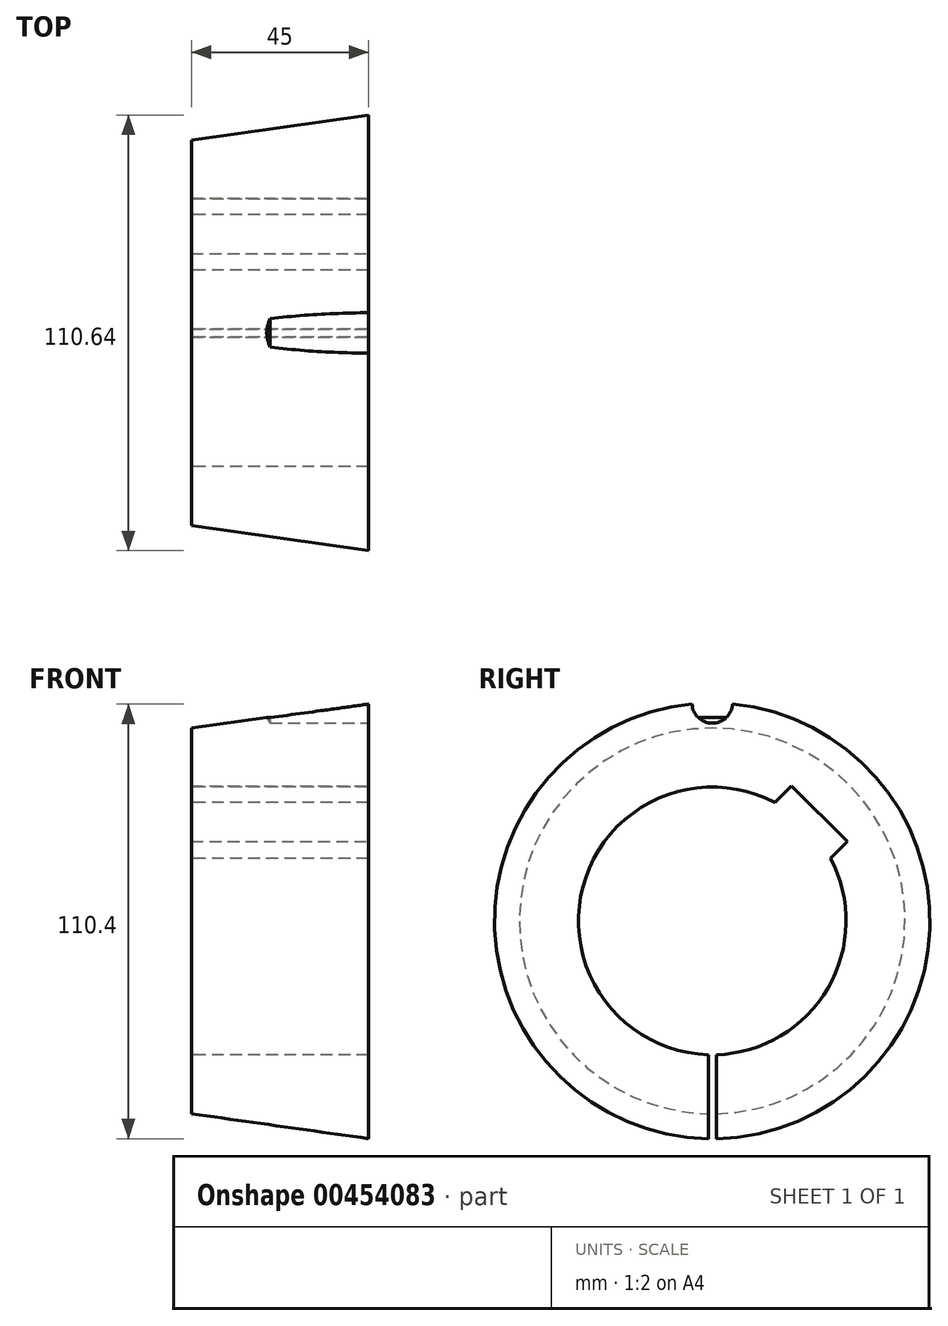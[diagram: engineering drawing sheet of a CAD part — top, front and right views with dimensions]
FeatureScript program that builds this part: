
annotation { "Feature Type Name" : "Feature", "Feature Type Description" : "" }
export const myFeature = defineFeature(function(context is Context, id is Id, definition is map)
    precondition{}
    {
        {
            var Q0;
            Q0=qCreatedBy(makeId("Front.planeOp"),FACE);
            var sketch = newSketch(context, id + "F0", { "sketchPlane" : qUnion([Q0])});
            skLineSegment(sketch, "E0", {"start": v(-22.5, 34) * mm, "end": v(22.5, 34) * mm});
            skLineSegment(sketch, "E1", {"start": v(22.5, 34) * mm, "end": v(22.5, 55.32) * mm});
            skLineSegment(sketch, "E2", {"start": v(22.5, 55.32) * mm, "end": v(-22.5, 49) * mm});
            skLineSegment(sketch, "E3", {"start": v(-22.5, 49) * mm, "end": v(-22.5, 34) * mm});
            skLineSegment(sketch, "E4", {"start": v(-52.72, 0) * mm, "end": v(58.36, 0) * mm, "construction": true});
            skSolve(sketch);
        }
        {
            var Q0;
            Q0=makeQuery(id+"F0.imprint","IMPRINT",FACE,{"disambiguationData":[TD([[makeQuery(id+"F0.imprint","IMPRINT",EDGE,{"derivedFrom":sQuery(id+"F0.wireOp",EDGE,"E0")}),1.0]])]});
            var Q1;
            Q1=sQuery(id+"F0.wireOp",EDGE,"E4");
            revolve(context, id + "F1", {"entities" : qUnion([Q0]), "axis" : qUnion([Q1]), "revolveType" : RevolveType.FULL});
        }
        {
            var Q0;
            Q0=makeQuery(id+"F1.opRevolve","SWEPT_FACE",FACE,{"disambiguationData":[OSD([sQuery(id+"F0.wireOp",EDGE,"E1")])]});
            var sketch = newSketch(context, id + "F2", { "sketchPlane" : qUnion([Q0])});
            skSolve(sketch);
        }
        {
            var Q0;
            {var subQ0=sQuery(id+"F0.wireOp",EDGE,"E1");Q0=makeQuery(id+"F2.imprint","IMPRINT",FACE,{"disambiguationData":[TD([[makeQuery(id+"F2.imprint","IMPRINT",EDGE,{"derivedFrom":makeQuery(id+"F1.opRevolve","SWEPT_EDGE",EDGE,{"disambiguationData":[OSD([sQuery(id+"F0.wireOp",EDGE,"E0"),subQ0])]})}),1.0]])]});}
            var sketch = newSketch(context, id + "F3", { "sketchPlane" : qUnion([Q0])});
            skLineSegment(sketch, "E5.bottom", {"start": v(-1, -29.74) * mm, "end": v(1, -29.74) * mm});
            skLineSegment(sketch, "E5.top", {"start": v(-1, -60.33) * mm, "end": v(1, -60.33) * mm});
            skLineSegment(sketch, "E5.left", {"start": v(1, -29.74) * mm, "end": v(1, -60.33) * mm});
            skLineSegment(sketch, "E5.right", {"start": v(-1, -29.74) * mm, "end": v(-1, -60.33) * mm});
            skSolve(sketch);
        }
        {
            var Q0;
            Q0 = qSketchRegion(id + "F3", true);
            extrude(context, id + "F4", {"entities" : qUnion([Q0]), "operationType" : NewBodyOperationType.REMOVE, "endBound" : BoundingType.THROUGH_ALL, "oppositeDirection" : true, "depth" : 25 * mm});
        }
        {
            var Q0;
            {var subQ0=sQuery(id+"F0.wireOp",EDGE,"E1");Q0=makeQuery(id+"F2.imprint","IMPRINT",FACE,{"disambiguationData":[TD([[makeQuery(id+"F2.imprint","IMPRINT",EDGE,{"derivedFrom":makeQuery(id+"F1.opRevolve","SWEPT_EDGE",EDGE,{"disambiguationData":[OSD([sQuery(id+"F0.wireOp",EDGE,"E0"),subQ0])]})}),1.0]])]});}
            var sketch = newSketch(context, id + "F5", { "sketchPlane" : qUnion([Q0])});
            skCircle(sketch, "E6", {"center": v(0, 0) * mm, "radius": 54 * mm, "construction": true});
            skCircle(sketch, "E7", {"center": v(0, 54) * mm, "radius": 6.25 * mm});
            skSolve(sketch);
        }
        {
            var Q0;
            {var subQ0=sQuery(id+"F0.wireOp",EDGE,"E1");Q0=makeQuery(id+"F2.imprint","IMPRINT",FACE,{"disambiguationData":[TD([[makeQuery(id+"F2.imprint","IMPRINT",EDGE,{"derivedFrom":makeQuery(id+"F1.opRevolve","SWEPT_EDGE",EDGE,{"disambiguationData":[OSD([sQuery(id+"F0.wireOp",EDGE,"E0"),subQ0])]})}),1.0]])]});}
            var sketch = newSketch(context, id + "F6", { "sketchPlane" : qUnion([Q0])});
            skLineSegment(sketch, "E8", {"start": v(0, 0) * mm, "end": v(39.94, 39.94) * mm, "construction": true});
            skArc(sketch, "E9.0", {"start": v(-1, -33.99) * mm, "mid": v(0, 34) * mm, "end": v(1, -33.99) * mm, "construction": true});
            skLineSegment(sketch, "E10.0", {"start": v(34.3, 20.15) * mm, "end": v(27.44, 13.3) * mm});
            skLineSegment(sketch, "E10.1", {"start": v(27.44, 13.3) * mm, "end": v(13.3, 27.44) * mm});
            skLineSegment(sketch, "E10.2", {"start": v(13.3, 27.44) * mm, "end": v(20.15, 34.3) * mm});
            skLineSegment(sketch, "E10.3", {"start": v(20.15, 34.3) * mm, "end": v(34.3, 20.15) * mm});
            skPoint(sketch, "E10.0.midPoint", {"position": v(30.87, 16.73) * mm});
            skArc(sketch, "E11.0", {"start": v(6.17, 54.98) * mm, "mid": v(55.26, -2.6) * mm, "end": v(1, -55.32) * mm});
            skSolve(sketch);
        }
        {
            var Q0;
            Q0 = qSketchRegion(id + "F6", true);
            extrude(context, id + "F7", {"entities" : qUnion([Q0]), "operationType" : NewBodyOperationType.REMOVE, "endBound" : BoundingType.THROUGH_ALL, "oppositeDirection" : true, "depth" : 25 * mm});
        }
        {
            var Q0;
            {var subQ0=sQuery(id+"F0.wireOp",EDGE,"E1");Q0=makeQuery(id+"F2.imprint","IMPRINT",FACE,{"disambiguationData":[TD([[makeQuery(id+"F2.imprint","IMPRINT",EDGE,{"derivedFrom":makeQuery(id+"F1.opRevolve","SWEPT_EDGE",EDGE,{"disambiguationData":[OSD([sQuery(id+"F0.wireOp",EDGE,"E0"),subQ0])]})}),1.0]])]});}
            var sketch = newSketch(context, id + "F8", { "sketchPlane" : qUnion([Q0])});
            skPoint(sketch, "E12", {"position": v(0, 55.4) * mm});
            skSolve(sketch);
        }
        {
            var Q0;
            Q0=sQuery(id+"F8.wireOp",VERTEX,"E12");
            var Q1;
            Q1=makeQuery(id+"F1.opRevolve","SWEPT_BODY",BODY,{"disambiguationData":[OSD([sQuery(id+"F0.wireOp",EDGE,"E0"),sQuery(id+"F0.wireOp",EDGE,"E1"),sQuery(id+"F0.wireOp",EDGE,"E2"),sQuery(id+"F0.wireOp",EDGE,"E3")])]});
            hole(context, id + "F9", {"style" : HoleStyle.SIMPLE, "endStyle" : HoleEndStyle.BLIND, "standardTappedOrClearance" : lookupTablePath({ "standard" : "ISO", "engagement" : "75%", "pitch" : "1.75 mm", "size" : "M12", "type" : "Tapped" }), "standardBlindInLast" : lookupTablePath({ "standard" : "ISO", "engagement" : "75%", "pitch" : "1.75 mm", "size" : "M12", "type" : "Tapped" }), "holeDiameter" : 10.3 * mm, "showTappedDepth" : true, "holeDepth" : 25 * mm, "isTappedThrough" : true, "tappedDepth" : 19.75 * mm, "tapClearance" : 3, "startFromSketch" : true, "locations" : qUnion([Q0]), "scope" : qUnion([Q1]), "majorDiameter" : 12 * mm});
        }
    });
